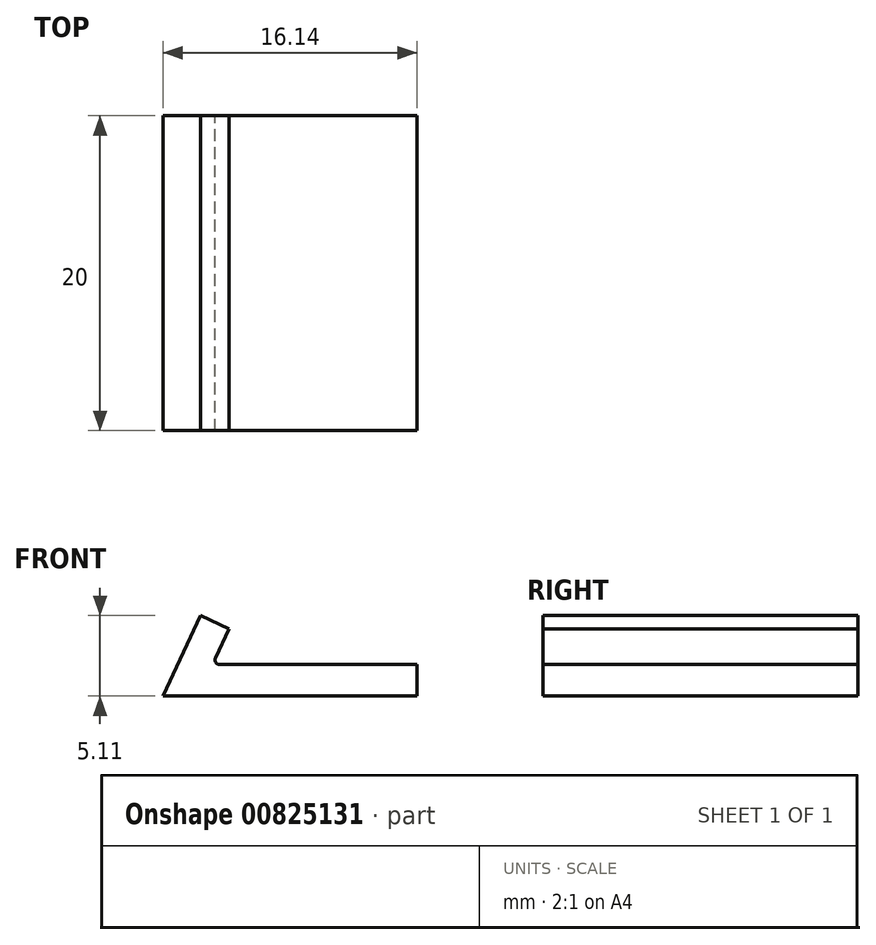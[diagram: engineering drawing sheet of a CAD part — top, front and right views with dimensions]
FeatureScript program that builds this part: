
annotation { "Feature Type Name" : "Feature", "Feature Type Description" : "" }
export const myFeature = defineFeature(function(context is Context, id is Id, definition is map)
    precondition{}
    {
        {
            var Q0;
            Q0=qCreatedBy(makeId("Front.planeOp"),FACE);
            var sketch = newSketch(context, id + "F0", { "sketchPlane" : qUnion([Q0])});
            skLineSegment(sketch, "E0", {"start": v(0, 0) * mm, "end": v(16.14, 0) * mm});
            skLineSegment(sketch, "E1", {"start": v(16.14, 0) * mm, "end": v(16.14, 2) * mm});
            skLineSegment(sketch, "E2", {"start": v(16.14, 2) * mm, "end": v(3.6, 2) * mm});
            skLineSegment(sketch, "E3", {"start": v(3.33, 2.42) * mm, "end": v(4.2, 4.27) * mm});
            skLineSegment(sketch, "E4", {"start": v(4.2, 4.27) * mm, "end": v(2.38, 5.11) * mm});
            skLineSegment(sketch, "E5", {"start": v(2.38, 5.11) * mm, "end": v(0, 0) * mm});
            skPoint(sketch, "E6.visualSharp", {"position": v(3.14, 2) * mm});
            skArc(sketch, "E6.filletArc", {"start": v(3.33, 2.42) * mm, "mid": v(3.35, 2.14) * mm, "end": v(3.6, 2) * mm});
            skSolve(sketch);
        }
        {
            var Q0;
            Q0 = qSketchRegion(id + "F0", true);
            extrude(context, id + "F1", {"entities" : qUnion([Q0]), "depth" : 20 * mm, "offsetDistance" : 25.4 * mm});
        }
    });
